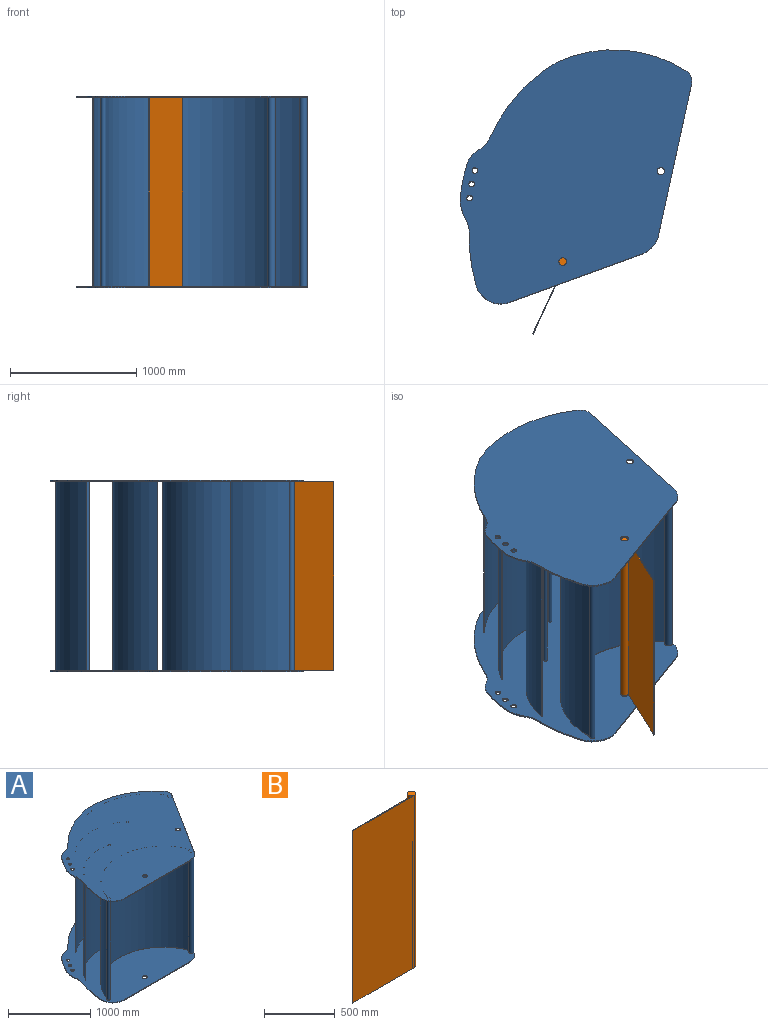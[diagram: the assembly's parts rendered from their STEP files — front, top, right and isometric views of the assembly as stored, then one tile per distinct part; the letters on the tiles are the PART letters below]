
ASSEMBLY  parts=2 mates=2
PART A: 61 faces, bbox 2164.2x1661x1520 mm
  f0: cylinder r=30.5mm len=61mm, axis (0,0,-1), area 1916.4mm2, adj f48,f49
  f1: cylinder r=29.5mm len=59mm, axis (0,0,-1), area 1853.5mm2, adj f48,f49
  f2: cylinder r=22mm len=44mm, axis (0,0,-1), area 1382.3mm2, adj f48,f49
  f3: cylinder r=22mm len=44mm, axis (0,0,-1), area 1382.3mm2, adj f48,f49
  f4: cylinder r=22mm len=44mm, axis (0,0,-1), area 1382.3mm2, adj f48,f49
  f5: cylinder r=326.18mm len=176.61mm, axis (0,0,-1), area 1797.7mm2, adj f48,f49,f50,f60
  f6: cylinder r=200mm len=212.82mm, axis (0,0,-1), area 3269.9mm2, adj f48,f49,f51,f52
  f7: cylinder r=20.5mm len=1500mm, axis (0,0,-1), area 183146.8mm2, adj f30,f44,f45,f49
  f8: cylinder r=30.5mm len=1500mm, axis (0,0,-1), area 272705.4mm2, adj f30,f44,f45,f46,f47,f49
  f9: cylinder r=15.5mm len=1500mm, axis (0,0,-1), area 135747.8mm2, adj f30,f41,f43,f49
  f10: cylinder r=15.5mm len=1500mm, axis (0,0,-1), area 136340.4mm2, adj f30,f37,f40,f49
  f11: cylinder r=30.5mm len=1500mm, axis (0,0,-1), area 274743.1mm2, adj f30,f32,f34,f35,f36,f49
  f12: cylinder r=30.5mm len=61mm, axis (0,0,-1), area 1916.4mm2, adj f30,f31
  f13: cylinder r=22mm len=44mm, axis (0,0,-1), area 1382.3mm2, adj f30,f31
  f14: cylinder r=22mm len=44mm, axis (0,0,-1), area 1382.3mm2, adj f30,f31
  f15: cylinder r=22mm len=44mm, axis (0,0,-1), area 1382.3mm2, adj f30,f31
  f16: cylinder r=29.5mm len=59mm, axis (0,0,-1), area 1853.5mm2, adj f30,f31
  f17: cylinder r=326.18mm len=176.61mm, axis (0,0,-1), area 1797.7mm2, adj f28,f29,f30,f31
  f18: cylinder r=200mm len=212.82mm, axis (0,0,-1), area 3269.9mm2, adj f19,f20,f30,f31
  f19: cylinder r=1403.06mm len=415.74mm, axis (0,0,-1), area 4273.2mm2, adj f18,f29,f30,f31
  f20: plane 1123.76x10mm, normal (0,-1,0), area 11237.6mm2, adj f18,f21,f30,f31
  f21: cylinder r=200mm len=169mm, axis (0,0,-1), area 2013.2mm2, adj f20,f22,f30,f31
  f22: plane 1036.5x655.9mm, normal (0.85,-0.53,0), area 12265.9mm2, adj f21,f23,f30,f31,f36,f47
  f23: cylinder r=100mm len=114.68mm, axis (0,0,-1), area 1222.9mm2, adj f22,f24,f30,f31
  f24: cylinder r=1074.34mm len=926.41mm, axis (0,0,-1), area 10568mm2, adj f23,f25,f30,f31
  f25: cylinder r=1282.61mm len=713.26mm, axis (0,0,-1), area 8227.7mm2, adj f24,f26,f30,f31
  f26: cylinder r=200mm len=117.51mm, axis (0,0,-1), area 1346.6mm2, adj f25,f27,f30,f31
  f27: cylinder r=186.95mm len=116.81mm, axis (0,0,-1), area 1363.1mm2, adj f26,f28,f30,f31
  f28: cylinder r=1324.47mm len=239.75mm, axis (0,0,-1), area 2828.3mm2, adj f17,f27,f30,f31
  f29: cylinder r=200mm len=107.43mm, axis (0,0,-1), area 1093.1mm2, adj f17,f19,f30,f31
  f30: plane 2164.16x1660.98mm, normal (0,0,1), area 2565292.9mm2, adj f7,f8,f9,f10,f11,f12,f13,f14
  f31: plane 2164.16x1660.98mm, normal (0,0,-1), area 2603609.2mm2, adj f12,f13,f14,f15,f16,f17,f18,f19
  f32: cylinder r=883.17mm len=1500mm, axis (0,0,-1), area 1936048.7mm2, adj f11,f30,f33,f49
  f33: plane 1500x5.5mm, normal (-0.92,-0.4,0), area 9000mm2, adj f30,f32,f34,f49
  f34: cylinder r=877.17mm len=1500mm, axis (0,0,-1), area 1914005.6mm2, adj f11,f30,f33,f49
  f35: plane 9.3x5.88mm, normal (0,0,1), area 3.7mm2, adj f11,f54
  f36: plane 9.3x5.88mm, normal (0,0,-1), area 3.7mm2, adj f11,f22
  f37: cylinder r=685.89mm len=1500mm, axis (0,0,-1), area 1444091.5mm2, adj f10,f30,f38,f49
  f38: plane 1500x4.62mm, normal (-0.77,-0.64,0), area 9000mm2, adj f30,f37,f39,f49
  f39: plane 1500x0.08mm, normal (0.65,-0.76,0), area 152.6mm2, adj f30,f38,f40,f49
  f40: cylinder r=679.89mm len=1500mm, axis (0,0,-1), area 1427930.9mm2, adj f10,f30,f39,f49
  f41: cylinder r=640.37mm len=1500mm, axis (0,0,-1), area 1242581.2mm2, adj f9,f30,f42,f49
  f42: plane 1500x5.24mm, normal (-0.49,-0.87,0), area 9000mm2, adj f30,f41,f43,f49
  f43: cylinder r=634.37mm len=1500mm, axis (0,0,-1), area 1226053.6mm2, adj f9,f30,f42,f49
  f44: cylinder r=755.25mm len=1500mm, axis (0,0,-1), area 2799788.5mm2, adj f7,f8,f30,f49
  f45: cylinder r=761.25mm len=1500mm, axis (0,0,-1), area 2838096.4mm2, adj f7,f8,f30,f49
  f46: plane 9.3x5.88mm, normal (0,0,1), area 3.7mm2, adj f8,f54
  f47: plane 9.3x5.88mm, normal (0,0,-1), area 3.7mm2, adj f8,f22
  f48: plane 2164.16x1660.98mm, normal (0,0,1), area 2603609.2mm2, adj f0,f1,f2,f3,f4,f5,f6,f50
  f49: plane 2164.16x1660.98mm, normal (0,0,-1), area 2565292.9mm2, adj f0,f1,f2,f3,f4,f5,f6,f7
  f50: cylinder r=200mm len=107.43mm, axis (0,0,-1), area 1093.1mm2, adj f5,f48,f49,f51
  f51: cylinder r=1403.06mm len=415.74mm, axis (0,0,-1), area 4273.2mm2, adj f6,f48,f49,f50
  f52: plane 1123.76x10mm, normal (0,-1,0), area 11237.6mm2, adj f6,f48,f49,f53
  f53: cylinder r=200mm len=169mm, axis (0,0,-1), area 2013.2mm2, adj f48,f49,f52,f54
  f54: plane 1036.5x655.9mm, normal (0.85,-0.53,0), area 12265.9mm2, adj f35,f46,f48,f49,f53,f55
  f55: cylinder r=100mm len=114.68mm, axis (0,0,-1), area 1222.9mm2, adj f48,f49,f54,f56
  f56: cylinder r=1074.34mm len=926.41mm, axis (0,0,-1), area 10568mm2, adj f48,f49,f55,f57
  f57: cylinder r=1282.61mm len=713.26mm, axis (0,0,-1), area 8227.7mm2, adj f48,f49,f56,f58
  f58: cylinder r=200mm len=117.51mm, axis (0,0,-1), area 1346.6mm2, adj f48,f49,f57,f59
  f59: cylinder r=186.95mm len=116.81mm, axis (0,0,-1), area 1363.1mm2, adj f48,f49,f58,f60
  f60: cylinder r=1324.47mm len=239.75mm, axis (0,0,-1), area 2828.3mm2, adj f5,f48,f49,f59
PART B: 6 faces, bbox 646.3x61x1490 mm
  f0: cylinder r=30.5mm len=1490mm, axis (0,0,-1), area 256544.7mm2, adj f1,f2,f4,f5
  f1: plane 1490x615.77mm, normal (0,-1,0), area 917501.9mm2, adj f0,f3,f4,f5
  f2: plane 1490x597.61mm, normal (0,1,0), area 890434.7mm2, adj f0,f3,f4,f5
  f3: plane 1490x6mm, normal (-1,0,0), area 8940mm2, adj f1,f2,f4,f5
  f4: plane 646.27x61mm, normal (0,0,1), area 6542.9mm2, adj f0,f1,f2,f3
  f5: plane 646.27x61mm, normal (0,0,-1), area 6542.9mm2, adj f0,f1,f2,f3
PLACE A rot(axis=(0,0,1),20deg) t=(0,0,-10)mm
PLACE B rot(axis=(0,0,1),65deg) t=(-734.43,339.66,-10)mm
MATE planar A.f0 <-> B.f0  axis (0,0,-1) through (-777.23,-716.71,750)mm
MATE revolute A.f0 <-> B.f0  axis (0,0,-1) through (-777.23,-716.71,750)mm
